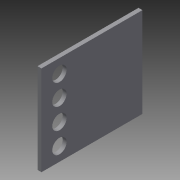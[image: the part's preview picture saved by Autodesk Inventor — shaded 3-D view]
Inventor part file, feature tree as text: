
AUTODESK INVENTOR PART (.ipt)
format: ipt  version: 2013 (Build 170138000, 138)  size: 89,600 bytes
history: native  units: mm
features: extrude x1, sketch x1
ambient origin geometry x8: Origin, YZ Plane, XZ Plane, XY Plane, X Axis, Y Axis, Z Axis, Center Point
feature tree (2):
  extrude  "Extrusion2"  Depth=500.0mm
  sketch  "Sketch4"  dims[d31=562.0mm d33=500.0mm d34=80.0mm d35=80.0mm d36=80.0mm d37=80.0mm d39=100.0mm d40=100.0mm d41=100.0mm d42=100.0mm d50=76.0mm d51=192.0mm d52=76.0mm d53=192.0mm d54=22.0mm d55=0.0mm]
